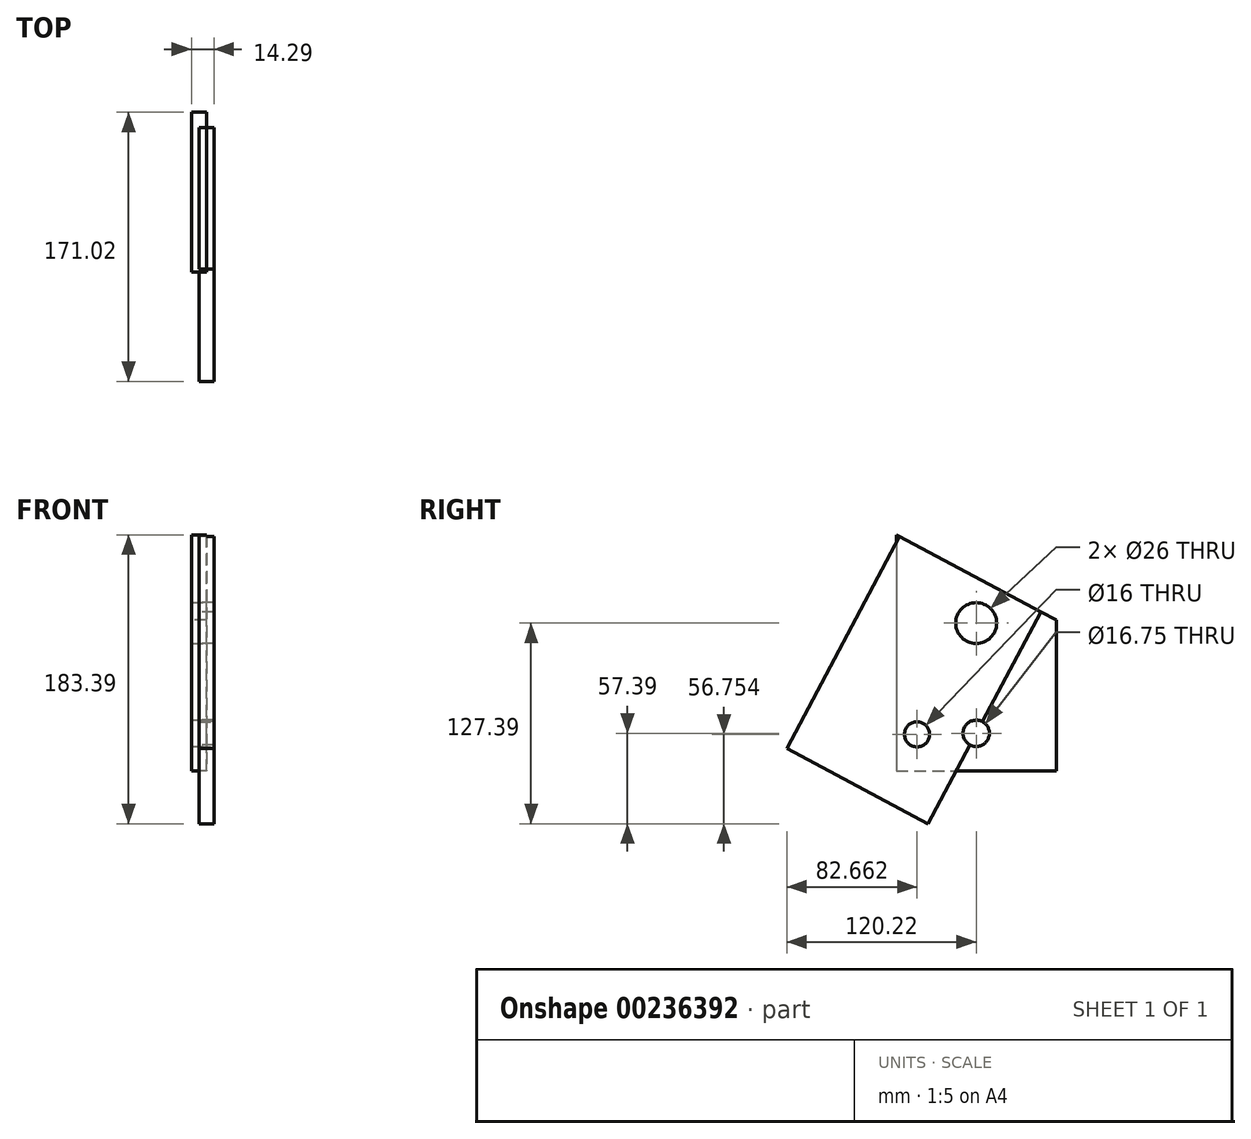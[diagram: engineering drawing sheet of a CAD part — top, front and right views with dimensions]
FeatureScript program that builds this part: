
annotation { "Feature Type Name" : "Feature", "Feature Type Description" : "" }
export const myFeature = defineFeature(function(context is Context, id is Id, definition is map)
    precondition{}
    {
        {
            var Q0;
            Q0=qCreatedBy(makeId("Right.planeOp"),FACE);
            var sketch = newSketch(context, id + "F0", { "sketchPlane" : qUnion([Q0])});
            skLineSegment(sketch, "E0", {"start": v(0, 0) * mm, "end": v(101.6, 0) * mm});
            skLineSegment(sketch, "E1", {"start": v(101.6, 0) * mm, "end": v(101.6, 95.98) * mm});
            skLineSegment(sketch, "E2", {"start": v(101.6, 95.98) * mm, "end": v(0, 150) * mm});
            skLineSegment(sketch, "E3", {"start": v(0, 150) * mm, "end": v(0, 0) * mm});
            skSolve(sketch);
        }
        {
            var Q0;
            Q0 = qSketchRegion(id + "F0", true);
            extrude(context, id + "F1", {"entities" : qUnion([Q0]), "endBound" : BoundingType.SYMMETRIC, "depth" : 9.52 * mm});
        }
        {
            var Q0;
            Q0=makeQuery(id+"F1.opExtrude","CAP_FACE",FACE,{"disambiguationData":[OSD([sQuery(id+"F0.wireOp",EDGE,"E0"),sQuery(id+"F0.wireOp",EDGE,"E1"),sQuery(id+"F0.wireOp",EDGE,"E2"),sQuery(id+"F0.wireOp",EDGE,"E3")])],"isStart":false});
            var sketch = newSketch(context, id + "F2", { "sketchPlane" : qUnion([Q0])});
            skPoint(sketch, "E4", {"position": v(50.8, 94) * mm});
            skPoint(sketch, "E5", {"position": v(50.8, 24) * mm});
            skLineSegment(sketch, "E6", {"start": v(50.8, 0) * mm, "end": v(50.8, 24) * mm});
            skLineSegment(sketch, "E7", {"start": v(50.8, 24) * mm, "end": v(50.8, 94) * mm});
            skSolve(sketch);
        }
        {
            var Q0;
            Q0=sQuery(id+"F2.wireOp",VERTEX,"E5");
            var Q1;
            Q1=makeQuery(id+"F1.opExtrude","SWEPT_BODY",BODY,{"disambiguationData":[OSD([sQuery(id+"F0.wireOp",EDGE,"E0"),sQuery(id+"F0.wireOp",EDGE,"E1"),sQuery(id+"F0.wireOp",EDGE,"E2"),sQuery(id+"F0.wireOp",EDGE,"E3")])]});
            hole(context, id + "F3", {"style" : HoleStyle.SIMPLE, "endStyle" : HoleEndStyle.THROUGH, "standardTappedOrClearance" : lookupTablePath({ "standard" : "ISO", "fit" : "Close", "size" : "M16", "type" : "Clearance" }), "standardBlindInLast" : lookupTablePath({ "fit" : "Close", "standard" : "ISO", "size" : "M16", "type" : "Clearance" }), "holeDiameter" : 16.75 * mm, "tappedDepth" : 12 * mm, "tapClearance" : 3, "locations" : qUnion([Q0]), "scope" : qUnion([Q1])});
        }
        {
            var Q0;
            Q0=sQuery(id+"F2.wireOp",VERTEX,"E4");
            var Q1;
            Q1=makeQuery(id+"F1.opExtrude","SWEPT_BODY",BODY,{"disambiguationData":[OSD([sQuery(id+"F0.wireOp",EDGE,"E0"),sQuery(id+"F0.wireOp",EDGE,"E1"),sQuery(id+"F0.wireOp",EDGE,"E2"),sQuery(id+"F0.wireOp",EDGE,"E3")])]});
            hole(context, id + "F4", {"style" : HoleStyle.SIMPLE, "endStyle" : HoleEndStyle.THROUGH, "holeDiameter" : 26 * mm, "tappedDepth" : 12 * mm, "tapClearance" : 3, "locations" : qUnion([Q0]), "scope" : qUnion([Q1])});
        }
        {
            var Q0;
            Q0=qCreatedBy(makeId("Right.planeOp"),FACE);
            var sketch = newSketch(context, id + "F5", { "sketchPlane" : qUnion([Q0])});
            skLineSegment(sketch, "E8", {"start": v(2.13, 148.87) * mm, "end": v(-69.42, 14.3) * mm});
            skLineSegment(sketch, "E9", {"start": v(-69.42, 14.3) * mm, "end": v(20.29, -33.39) * mm});
            skLineSegment(sketch, "E10", {"start": v(20.29, -33.39) * mm, "end": v(46.87, 16.6) * mm});
            skLineSegment(sketch, "E11", {"start": v(91.83, 101.17) * mm, "end": v(2.13, 148.87) * mm});
            skCircle(sketch, "E12.0", {"center": v(50.8, 94) * mm, "radius": 13 * mm});
            skArc(sketch, "E13.0", {"start": v(54.73, 31.4) * mm, "mid": v(43.4, 27.93) * mm, "end": v(46.87, 16.6) * mm});
            skLineSegment(sketch, "E14.trimOffspring", {"start": v(54.73, 31.4) * mm, "end": v(91.83, 101.17) * mm});
            skSolve(sketch);
        }
        {
            var Q0;
            Q0=makeQuery(id+"F5.imprint","IMPRINT",FACE,{"disambiguationData":[TD([[makeQuery(id+"F5.imprint","IMPRINT",EDGE,{"derivedFrom":sQuery(id+"F5.wireOp",EDGE,"E8")}),1.0]])]});
            extrude(context, id + "F6", {"entities" : qUnion([Q0]), "depth" : 9.52 * mm});
        }
        {
            var Q0;
            Q0=makeQuery(id+"F6.opExtrude","CAP_FACE",FACE,{"disambiguationData":[OSD([sQuery(id+"F5.wireOp",EDGE,"E8"),sQuery(id+"F5.wireOp",EDGE,"E9"),sQuery(id+"F5.wireOp",EDGE,"E10"),sQuery(id+"F5.wireOp",EDGE,"E11"),sQuery(id+"F5.wireOp",EDGE,"E12.0"),sQuery(id+"F5.wireOp",EDGE,"E13.0"),sQuery(id+"F5.wireOp",EDGE,"E14.trimOffspring")])],"isStart":false});
            var sketch = newSketch(context, id + "F7", { "sketchPlane" : qUnion([Q0])});
            skLineSegment(sketch, "E15", {"start": v(50.8, 94) * mm, "end": v(13.24, 23.36) * mm});
            skSolve(sketch);
        }
        {
            var Q0;
            Q0=sQuery(id+"F7.wireOp",VERTEX,"E15.end");
            var Q1;
            Q1=makeQuery(id+"F6.opExtrude","SWEPT_BODY",BODY,{"disambiguationData":[OSD([sQuery(id+"F5.wireOp",EDGE,"E8"),sQuery(id+"F5.wireOp",EDGE,"E9"),sQuery(id+"F5.wireOp",EDGE,"E10"),sQuery(id+"F5.wireOp",EDGE,"E11"),sQuery(id+"F5.wireOp",EDGE,"E12.0"),sQuery(id+"F5.wireOp",EDGE,"E13.0"),sQuery(id+"F5.wireOp",EDGE,"E14.trimOffspring")])]});
            hole(context, id + "F8", {"style" : HoleStyle.SIMPLE, "endStyle" : HoleEndStyle.THROUGH, "holeDiameter" : 16 * mm, "tappedDepth" : 12 * mm, "tapClearance" : 3, "locations" : qUnion([Q0]), "scope" : qUnion([Q1])});
        }
    });
